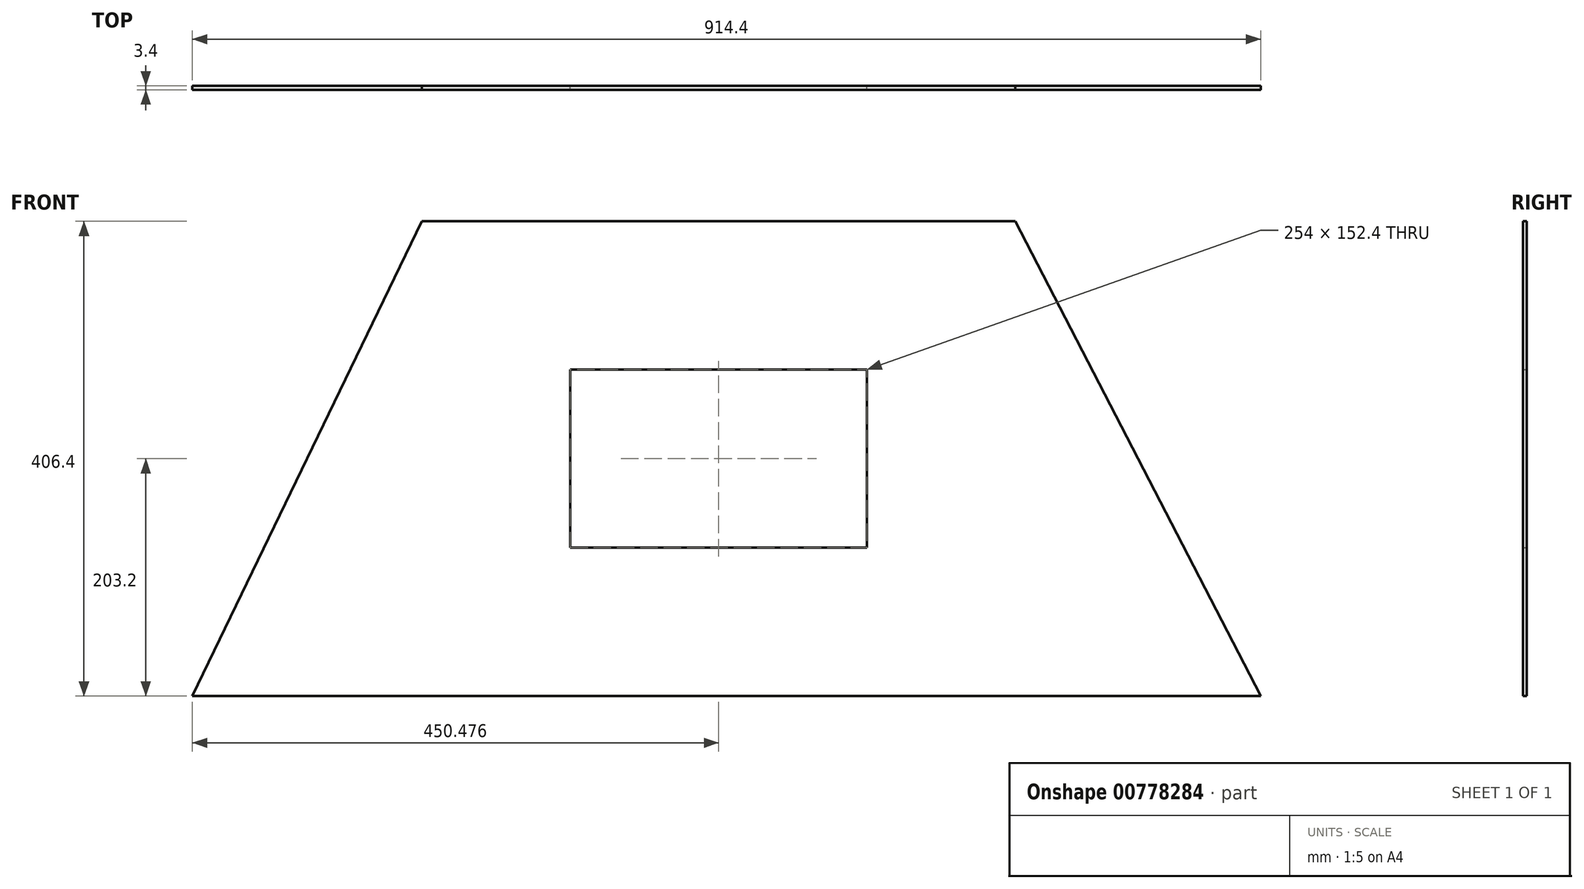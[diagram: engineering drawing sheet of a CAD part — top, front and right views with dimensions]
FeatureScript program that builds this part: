
annotation { "Feature Type Name" : "Feature", "Feature Type Description" : "" }
export const myFeature = defineFeature(function(context is Context, id is Id, definition is map)
    precondition{}
    {
        {
            var Q0;
            Q0=qCreatedBy(makeId("Front.planeOp"),FACE);
            var sketch = newSketch(context, id + "F0", { "sketchPlane" : qUnion([Q0])});
            skLineSegment(sketch, "E0", {"start": v(0, 0) * mm, "end": v(914.4, 0) * mm});
            skLineSegment(sketch, "E1", {"start": v(914.4, 0) * mm, "end": v(704.48, 406.4) * mm});
            skLineSegment(sketch, "E2", {"start": v(704.48, 406.4) * mm, "end": v(196.48, 406.4) * mm});
            skLineSegment(sketch, "E3", {"start": v(196.48, 406.4) * mm, "end": v(0, 0) * mm});
            skPoint(sketch, "E4", {"position": v(450.48, 203.2) * mm});
            skLineSegment(sketch, "E5.bottom", {"start": v(323.48, 279.4) * mm, "end": v(577.48, 279.4) * mm});
            skLineSegment(sketch, "E5.top", {"start": v(323.48, 127) * mm, "end": v(577.48, 127) * mm});
            skLineSegment(sketch, "E5.left", {"start": v(323.48, 279.4) * mm, "end": v(323.48, 127) * mm});
            skLineSegment(sketch, "E5.right", {"start": v(577.48, 279.4) * mm, "end": v(577.48, 127) * mm});
            skSolve(sketch);
        }
        {
            var Q0;
            Q0=qSketchRegion(id+"F0",true);
            var Q1;
            {var subQ0=sQuery(id+"F0.wireOp",EDGE,"ff04ecd3-62dd-4f04-a5e1-9ba258711f50.0");var subQ1=sQuery(id+"F0.wireOp",EDGE,"HUmVhOKA-ckSa-zBvS-Fccu-Swr1TjOunzXe");var subQ2=makeQuery(id+"F0.imprint","INTERSECT",VERTEX,{"disambiguationData":[OD(0.0)],"derivedFrom":[subQ1,subQ0]});Q1=makeQuery(id+"F0.imprint","IMPRINT",FACE,{"disambiguationData":[TD([[makeQuery(id+"F0.imprint","IMPRINT",EDGE,{"disambiguationData":[TD([[subQ2,1.0]])],"derivedFrom":subQ1}),-1.0]])]});}
            var Q2;
            {var subQ0=sQuery(id+"F0.wireOp",EDGE,"ff04ecd3-62dd-4f04-a5e1-9ba258711f50.2");var subQ1=sQuery(id+"F0.wireOp",EDGE,"HUmVhOKA-ckSa-zBvS-Fccu-Swr1TjOunzXe");var subQ2=makeQuery(id+"F0.imprint","INTERSECT",VERTEX,{"disambiguationData":[OD(1.0)],"derivedFrom":[subQ1,subQ0]});Q2=makeQuery(id+"F0.imprint","IMPRINT",FACE,{"disambiguationData":[TD([[makeQuery(id+"F0.imprint","IMPRINT",EDGE,{"disambiguationData":[TD([[subQ2,-1.0]])],"derivedFrom":subQ1}),-1.0]])]});}
            var Q3;
            {var subQ0=sQuery(id+"F0.wireOp",EDGE,"ff04ecd3-62dd-4f04-a5e1-9ba258711f50.0");var subQ1=sQuery(id+"F0.wireOp",EDGE,"HUmVhOKA-ckSa-zBvS-Fccu-Swr1TjOunzXe");var subQ2=makeQuery(id+"F0.imprint","INTERSECT",VERTEX,{"disambiguationData":[OD(1.0)],"derivedFrom":[subQ1,subQ0]});Q3=makeQuery(id+"F0.imprint","IMPRINT",FACE,{"disambiguationData":[TD([[makeQuery(id+"F0.imprint","IMPRINT",EDGE,{"disambiguationData":[TD([[subQ2,-1.0]])],"derivedFrom":subQ1}),-1.0]])]});}
            extrude(context, id + "F1", {"entities" : qUnion([Q0, Q1, Q2, Q3]), "depth" : 3.4 * mm, "offsetDistance" : 25.4 * mm});
        }
    });
